# Revit family: ShowerSet-PureHandShowerSet-Vitra-ShowerSystems-A45543
name_source: partatom
category: Plumbing Fixtures
revit_build: Autodesk Revit 2017 (Build: 20160225_1515(x64)
units: mm (PartAtom-declared; Revit-internal decimal feet)

## family parameters
Cut with Voids When Loaded = No
Host = Face
OmniClass Number = 23.45.05.14.17
OmniClass Title = Showers
Part Type = Normal
Room Calculation Point = No
Round Connector Dimension = Use Diameter
Shared = Yes

## types (12) — shared parameters
BIMobject category = Showers
Brand = VitrA
CW Connection = No
Connection Diameter (mm) = 15 mm  [stored 0.0492126 ft]
Default Elevation = 2000 mm
Description = ShowerSystems Pure Handshower Set
Design country = Turkey
HW Connection = No
Hot Water Supply (max.) = 80 °C
Hot Water temperature, factory set to = 38 °C
IFC Classification = Sanitary Terminal
Manufacturer = VitrA
Manufacturer name = VitrA
Min. flow pressure of = 0.5 bar
Mounting type = Wall Mopunted
NBS Referans Code = 35-06-81
NBS Referans Description = ShowerHeads
Nominal Depth (mm) = 80 mm
Nominal Height (mm) = 490 mm  [stored 1.60761 ft]
Nominal Width (mm) = 100 mm  [stored 0.328084 ft]
Number Of Connections = 1
OmniClass Code = 23-31 17 00
OmniClass Description = Showers
Product Type = Built-in Handshower Set
Product certification = https://www.vitraglobal.com
Product family = ShowerSystems
Product group = Handshower Set
Range of Hot Water Supply = 5 - 65 °C
Range of flow pressure = 1 - 5 bar
Technical description = https://www.vitraglobal.com
Test Pressure = 16 bar
URL = https://vitraglobal.com
Uniclass 1.4 Code = L7214
Uniclass 1.4 Description = Showers
Uniclass 2.0 Code = PR-35-06-81
Uniclass 2.0 Description = Shower Heads
Uniclass 2015 Code = Pr_40_20_87_77
Uniclass 2015 Name = Shower head holders
Uniformat II Description = FURNISHINGS
Vent Connection = No
Warranty Period (Year) = 5 years
Waste Connection = No
Weight Net (kg) = 0.9
Youtube = https://www.youtube.com

## per-type parameters (varying)
| type | Article No. (default) | Coating Material | Color | Model | Product SKU | Product data url |
| HandshowerSet-Vitra-ShowerSystems-A45543IND | A45543IND | Chrome | Chrome | A45543IND | A45543IND | https://www.vitraglobal.com |
| HandshowerSet-Vitra-ShowerSystems-A45543EXP | A45543EXP | Chrome | Chrome | A45543EXP | A45543EXP | https://www.vitraglobal.com |
| HandshowerSet-Vitra-ShowerSystems-A4554337 | A4554337 | Brushed Nickel | Brushed Nickel | A4554337 | A4554337 | https://www.vitraglobal.com |
| HandshowerSet-Vitra-ShowerSystems-A4554336IND | A4554336IND | Matte Black | Matte Black | A4554336IND | A4554336IND | https://www.vitraglobal.com |
| HandshowerSet-Vitra-ShowerSystems-A4554336 | A4554336 | Matte Black | Matte Black | A4554336 | A4554336 | https://www.vitra.com.tr |
| HandshowerSet-Vitra-ShowerSystems-A4554334IND | A4554334IND | Nickel | Nickel | A4554334IND | A4554334IND | https://www.vitraglobal.com |
| HandshowerSet-Vitra-ShowerSystems-A4554334 | A4554334 | Nickel | Nickel | A4554334 | A4554334 | https://www.vitra.com.tr |
| HandshowerSet-Vitra-ShowerSystems-A4554333 | A4554333 | BrushedGold | Brushed Gold | A4554333 | A4554333 | https://www.vitraglobal.com |
| HandshowerSet-Vitra-ShowerSystems-A4554326IND | A4554326IND | BrightCopper | Copper | A4554326IND | A4554326IND | https://www.vitraglobal.com |
| HandshowerSet-Vitra-ShowerSystems-A4554326 | A4554326 | BrightCopper | Copper | A4554326 | A4554326 | https://www.vitra.com.tr |
| HandshowerSet-Vitra-ShowerSystems-A4554323 | A4554323 | Gold | Gold | A4554323 | A4554323 | https://www.vitraglobal.com |
| HandshowerSet-Vitra-ShowerSystems-A45543 | A45543 | Chrome | Chrome | A45543 | A45543 | https://www.vitraglobal.com |

note: [stored X ft] marks values corroborated as IEEE doubles in the binary element streams (Revit-internal decimal feet)

## geometry (parser evidence)
native form markers: Sweep x2
no freeform markers — native parametric forms only
